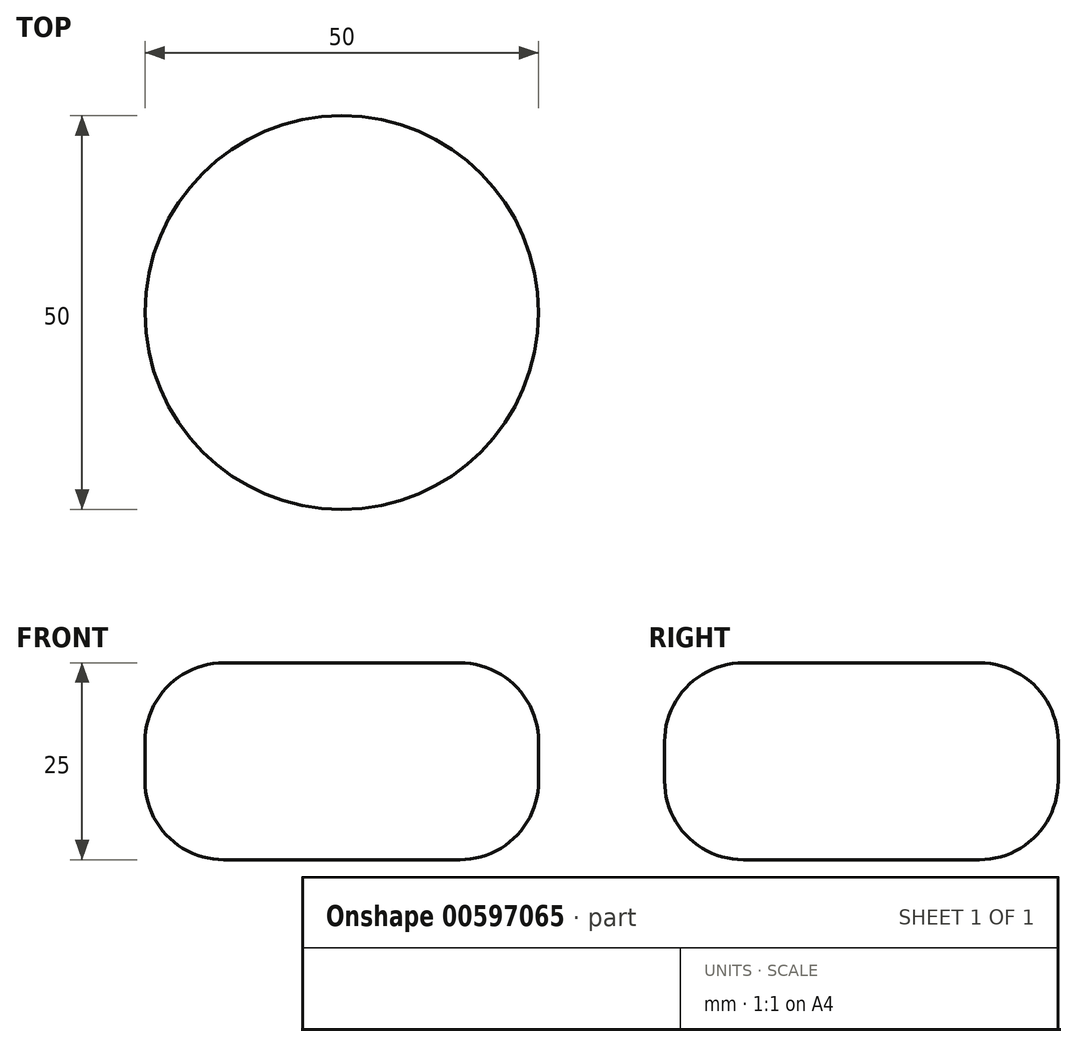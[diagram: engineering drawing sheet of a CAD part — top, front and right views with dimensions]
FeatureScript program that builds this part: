
annotation { "Feature Type Name" : "Feature", "Feature Type Description" : "" }
export const myFeature = defineFeature(function(context is Context, id is Id, definition is map)
    precondition{}
    {
        {
            var Q0;
            Q0=qCreatedBy(makeId("Top.planeOp"),FACE);
            var sketch = newSketch(context, id + "F0", { "sketchPlane" : qUnion([Q0])});
            skCircle(sketch, "E0", {"center": v(0, 0) * mm, "radius": 25 * mm});
            skSolve(sketch);
        }
        {
            var Q0;
            Q0=makeQuery(id+"F0.imprint","IMPRINT",FACE,{"disambiguationData":[TD([[makeQuery(id+"F0.imprint","IMPRINT",EDGE,{"derivedFrom":sQuery(id+"F0.wireOp",EDGE,"E0")}),1.0]])]});
            extrude(context, id + "F1", {"entities" : qUnion([Q0]), "endBound" : BoundingType.SYMMETRIC, "depth" : 25 * mm, "offsetDistance" : 25 * mm});
        }
        {
            var Q0;
            Q0=makeQuery(id+"F1.opExtrude","CAP_EDGE",EDGE,{"disambiguationData":[OSD([sQuery(id+"F0.wireOp",EDGE,"E0")])],"isStart":false});
            var Q1;
            Q1=makeQuery(id+"F1.opExtrude","CAP_EDGE",EDGE,{"disambiguationData":[OSD([sQuery(id+"F0.wireOp",EDGE,"E0")])],"isStart":true});
            fillet(context, id + "F2", {"entities" : qUnion([Q0, Q1]), "radius" : 10 * mm, "tangentPropagation" : true, "allowEdgeOverflow" : false});
        }
    });
